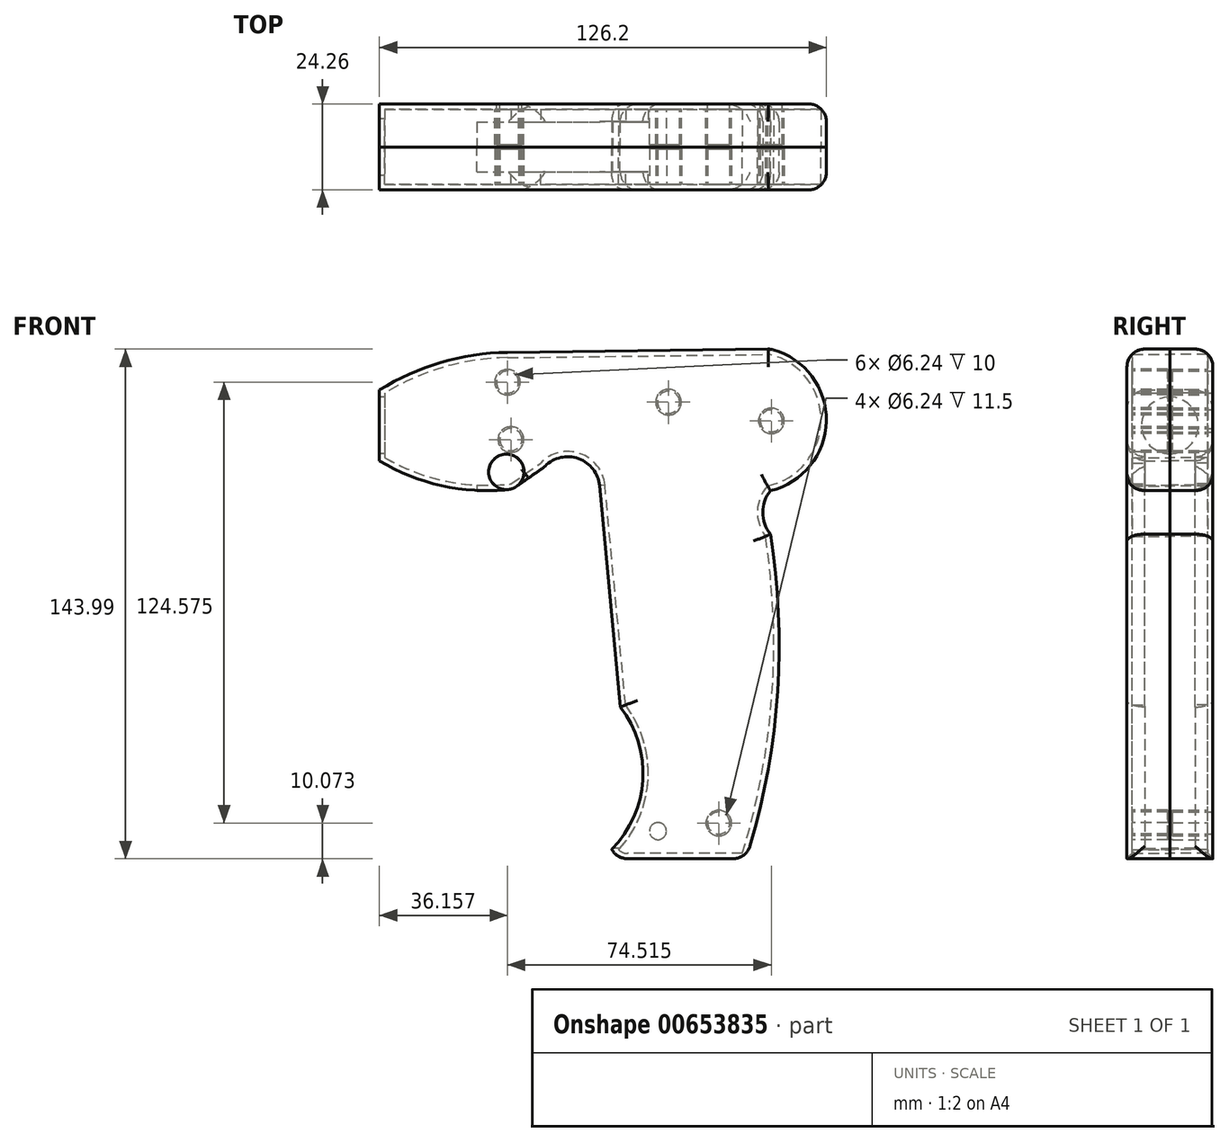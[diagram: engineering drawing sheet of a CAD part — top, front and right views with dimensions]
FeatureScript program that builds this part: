
annotation { "Feature Type Name" : "Feature", "Feature Type Description" : "" }
export const myFeature = defineFeature(function(context is Context, id is Id, definition is map)
    precondition{}
    {
        {
            var Q0;
            Q0=qCreatedBy(makeId("Front.planeOp"),FACE);
            var sketch = newSketch(context, id + "F0", { "sketchPlane" : qUnion([Q0])});
            skLineSegment(sketch, "E0", {"start": v(-46.5, 40.72) * mm, "end": v(-46.5, 20.76) * mm});
            skArc(sketch, "E1", {"start": v(63.9, 12.29) * mm, "mid": v(79.7, 32.29) * mm, "end": v(63.9, 52.29) * mm});
            skPoint(sketch, "E2", {"position": v(65.78, -46.25) * mm});
            skPoint(sketch, "E3", {"position": v(89.04, 165.66) * mm});
            skPoint(sketch, "E4", {"position": v(-8.84, 12.76) * mm});
            skPoint(sketch, "E5", {"position": v(-8.84, 20.76) * mm});
            skPoint(sketch, "E6", {"position": v(79.7, 32.29) * mm});
            skArc(sketch, "E7", {"start": v(63.9, 12.29) * mm, "mid": v(61.71, 6.14) * mm, "end": v(63.9, 0) * mm});
            skArc(sketch, "E8", {"start": v(57.05, -91.71) * mm, "mid": v(65.78, -46.25) * mm, "end": v(63.9, 0) * mm});
            skLineSegment(sketch, "E9", {"start": v(57.05, -91.71) * mm, "end": v(23.56, -91.71) * mm});
            skLineSegment(sketch, "E10", {"start": v(21.52, -48.85) * mm, "end": v(15.66, 13.67) * mm});
            skLineSegment(sketch, "E11", {"start": v(-10.37, 51.36) * mm, "end": v(63.9, 52.29) * mm});
            skPoint(sketch, "E12", {"position": v(57.05, -91.71) * mm});
            skLineSegment(sketch, "E13", {"start": v(-8.84, 12.76) * mm, "end": v(0, 18.96) * mm});
            skArc(sketch, "E14", {"start": v(15.66, 13.67) * mm, "mid": v(9.55, 21.4) * mm, "end": v(0, 18.96) * mm});
            skArc(sketch, "E15", {"start": v(19.1, -89.07) * mm, "mid": v(20.97, -91) * mm, "end": v(23.56, -91.71) * mm});
            skArc(sketch, "E16", {"start": v(19.1, -89.07) * mm, "mid": v(27.84, -69.42) * mm, "end": v(21.52, -48.85) * mm});
            skPoint(sketch, "E17", {"position": v(19.1, -91.71) * mm});
            skArc(sketch, "E18", {"start": v(-46.5, 20.76) * mm, "mid": v(-28.35, 13.58) * mm, "end": v(-8.84, 12.76) * mm});
            skArc(sketch, "E19", {"start": v(-10.37, 51.36) * mm, "mid": v(-29.17, 48.53) * mm, "end": v(-46.5, 40.72) * mm});
            skPoint(sketch, "E20", {"position": v(-10.37, 40.72) * mm});
            skPoint(sketch, "E21", {"position": v(63.9, 32.29) * mm});
            skPoint(sketch, "E22", {"position": v(60.43, -79.71) * mm});
            skPoint(sketch, "E23", {"position": v(40.05, -91.71) * mm});
            skPoint(sketch, "E24", {"position": v(40.05, -79.71) * mm});
            skPoint(sketch, "E25", {"position": v(-46.5, 30.74) * mm});
            skLineSegment(sketch, "E26", {"start": v(78.94, 37.8) * mm, "end": v(79.7, 32.29) * mm});
            skPoint(sketch, "E27", {"position": v(50.96, -79.71) * mm});
            skSolve(sketch);
        }
        {
            var Q0;
            Q0 = qSketchRegion(id + "F0", true);
            extrude(context, id + "F1", {"entities" : qUnion([Q0]), "depth" : 12.13 * mm, "offsetDistance" : 25 * mm});
        }
        {
            var Q0;
            Q0=makeQuery(id+"F1.opExtrude","CAP_FACE",FACE,{"disambiguationData":[OSD([sQuery(id+"F0.wireOp",EDGE,"E0"),sQuery(id+"F0.wireOp",EDGE,"E1"),sQuery(id+"F0.wireOp",EDGE,"E7"),sQuery(id+"F0.wireOp",EDGE,"E8"),sQuery(id+"F0.wireOp",EDGE,"E9"),sQuery(id+"F0.wireOp",EDGE,"E10"),sQuery(id+"F0.wireOp",EDGE,"E11"),sQuery(id+"F0.wireOp",EDGE,"E13"),sQuery(id+"F0.wireOp",EDGE,"E14"),sQuery(id+"F0.wireOp",EDGE,"E15"),sQuery(id+"F0.wireOp",EDGE,"E16"),sQuery(id+"F0.wireOp",EDGE,"E18"),sQuery(id+"F0.wireOp",EDGE,"E19")])],"isStart":true});
            shell(context, id + "F2", {"entities" : qUnion([Q0]), "thickness" : 1.5 * mm});
        }
        {
            var Q0;
            Q0=makeQuery(id+"F1.opExtrude","CAP_EDGE",EDGE,{"disambiguationData":[OSD([sQuery(id+"F0.wireOp",EDGE,"E11")])],"isStart":false});
            fillet(context, id + "F3", {"entities" : qUnion([Q0]), "radius" : 5 * mm, "tangentPropagation" : true, "allowEdgeOverflow" : false});
        }
        {
            var Q0;
            Q0=makeQuery(id+"F1.opExtrude","CAP_EDGE",EDGE,{"disambiguationData":[OSD([sQuery(id+"F0.wireOp",EDGE,"E1")])],"isStart":false});
            var Q1;
            Q1=makeQuery(id+"F1.opExtrude","CAP_EDGE",EDGE,{"disambiguationData":[OSD([sQuery(id+"F0.wireOp",EDGE,"E7")])],"isStart":false});
            var Q2;
            Q2=makeQuery(id+"F1.opExtrude","CAP_EDGE",EDGE,{"disambiguationData":[OSD([sQuery(id+"F0.wireOp",EDGE,"E8")])],"isStart":false});
            var Q3;
            Q3=makeQuery(id+"F1.opExtrude","SWEPT_EDGE",EDGE,{"disambiguationData":[OSD([sQuery(id+"F0.wireOp",EDGE,"E8"),sQuery(id+"F0.wireOp",EDGE,"E9")])]});
            var Q4;
            Q4=makeQuery(id+"F1.opExtrude","SWEPT_EDGE",EDGE,{"disambiguationData":[OSD([sQuery(id+"F0.wireOp",EDGE,"E9"),sQuery(id+"F0.wireOp",EDGE,"E15")])]});
            var Q5;
            Q5=makeQuery(id+"F1.opExtrude","CAP_EDGE",EDGE,{"disambiguationData":[OSD([sQuery(id+"F0.wireOp",EDGE,"E16")])],"isStart":false});
            var Q6;
            Q6=makeQuery(id+"F1.opExtrude","CAP_EDGE",EDGE,{"disambiguationData":[OSD([sQuery(id+"F0.wireOp",EDGE,"E10")])],"isStart":false});
            var Q7;
            Q7=makeQuery(id+"F1.opExtrude","CAP_EDGE",EDGE,{"disambiguationData":[OSD([sQuery(id+"F0.wireOp",EDGE,"E18")])],"isStart":false});
            var Q8;
            Q8=makeQuery(id+"F1.opExtrude","SWEPT_EDGE",EDGE,{"disambiguationData":[OSD([sQuery(id+"F0.wireOp",EDGE,"E13"),sQuery(id+"F0.wireOp",EDGE,"E18")])]});
            var Q9;
            Q9=makeQuery(id+"F1.opExtrude","SWEPT_EDGE",EDGE,{"disambiguationData":[OSD([sQuery(id+"F0.wireOp",EDGE,"E13"),sQuery(id+"F0.wireOp",EDGE,"E14")])]});
            fillet(context, id + "F4", {"entities" : qUnion([Q0, Q1, Q2, Q3, Q4, Q5, Q6, Q7, Q8, Q9]), "radius" : 5 * mm, "tangentPropagation" : true, "allowEdgeOverflow" : false});
        }
        {
            var Q0;
            Q0=makeQuery(id+"F1.opExtrude","SWEPT_FACE",FACE,{"disambiguationData":[OSD([sQuery(id+"F0.wireOp",EDGE,"E0")])]});
            var sketch = newSketch(context, id + "F5", { "sketchPlane" : qUnion([Q0])});
            skCircle(sketch, "E28", {"center": v(0, 30.74) * mm, "radius": 8 * mm});
            skSolve(sketch);
        }
        {
            var Q0;
            {var subQ0=sQuery(id+"F5.wireOp",EDGE,"E28");var subQ1=makeQuery(id+"F1.opExtrude","CAP_EDGE",EDGE,{"disambiguationData":[OSD([sQuery(id+"F0.wireOp",EDGE,"E0")])],"isStart":true});var subQ2=makeQuery(id+"F5.imprint","INTERSECT",VERTEX,{"disambiguationData":[OD(0.0)],"derivedFrom":[subQ1,subQ0]});Q0=makeQuery(id+"F5.imprint","IMPRINT",FACE,{"disambiguationData":[TD([[makeQuery(id+"F5.imprint","IMPRINT",EDGE,{"disambiguationData":[TD([[subQ2,1.0]])],"derivedFrom":subQ0}),1.0]])]});}
            extrude(context, id + "F6", {"entities" : qUnion([Q0]), "operationType" : NewBodyOperationType.REMOVE, "oppositeDirection" : true, "depth" : 25.5 * mm, "offsetDistance" : 25 * mm});
        }
        {
            var Q0;
            Q0=makeQuery(id+"F1.opExtrude","SWEPT_FACE",FACE,{"disambiguationData":[OSD([sQuery(id+"F0.wireOp",EDGE,"E10")])]});
            extrude(context, id + "F7", {"entities" : qUnion([Q0]), "operationType" : NewBodyOperationType.REMOVE, "oppositeDirection" : true, "depth" : 25 * mm, "offsetDistance" : 25 * mm});
        }
        {
            var Q0;
            Q0=qCreatedBy(makeId("Right.planeOp"),FACE);
            var sketch = newSketch(context, id + "F8", { "sketchPlane" : qUnion([Q0])});
            skLineSegment(sketch, "E29.bottom", {"start": v(0, 32.22) * mm, "end": v(-7.06, 32.22) * mm});
            skLineSegment(sketch, "E29.top", {"start": v(0, -88.8) * mm, "end": v(-7.06, -88.8) * mm});
            skLineSegment(sketch, "E29.left", {"start": v(0, 32.22) * mm, "end": v(0, -88.8) * mm});
            skLineSegment(sketch, "E29.right", {"start": v(-7.06, 32.22) * mm, "end": v(-7.06, -88.8) * mm});
            skSolve(sketch);
        }
        {
            var Q0;
            Q0 = qSketchRegion(id + "F8", true);
            extrude(context, id + "F9", {"entities" : qUnion([Q0]), "operationType" : NewBodyOperationType.REMOVE, "depth" : 32 * mm, "offsetDistance" : 25 * mm});
        }
        {
            var Q0;
            Q0=qCreatedBy(makeId("Right.planeOp"),FACE);
            var sketch = newSketch(context, id + "F10", { "sketchPlane" : qUnion([Q0])});
            skLineSegment(sketch, "E30.bottom", {"start": v(-7.06, 30.82) * mm, "end": v(0, 30.82) * mm});
            skLineSegment(sketch, "E30.top", {"start": v(-7.06, -88.82) * mm, "end": v(0, -88.82) * mm});
            skLineSegment(sketch, "E30.left", {"start": v(-7.06, 30.82) * mm, "end": v(-7.06, -88.82) * mm});
            skLineSegment(sketch, "E30.right", {"start": v(0, 30.82) * mm, "end": v(0, -88.82) * mm});
            skSolve(sketch);
        }
        {
            var Q0;
            Q0 = qSketchRegion(id + "F10", true);
            extrude(context, id + "F11", {"entities" : qUnion([Q0]), "operationType" : NewBodyOperationType.REMOVE, "oppositeDirection" : true, "depth" : 19 * mm, "offsetDistance" : 25 * mm});
        }
        {
            var Q0;
            {var subQ0=sQuery(id+"F0.wireOp",EDGE,"Wmh0p9kF-q8zf-B4fM-R1G6-9XajL4hFd1sJ");var subQ1=sQuery(id+"F0.wireOp",EDGE,"YQ1TRmyh-YhWL-v7ih-TSwX-I9xARRby4IsQ");var subQ2=sQuery(id+"F0.wireOp",EDGE,"R5RoQ8MB-LLDK-kKnW-gyy2-uW1s3o3SLSVy");var subQ3=sQuery(id+"F0.wireOp",EDGE,"7nFK0jpW-g7ep-zzM4-bCTe-Nh05jLanKP2S");var subQ4=sQuery(id+"F0.wireOp",EDGE,"E19");var subQ5=sQuery(id+"F0.wireOp",EDGE,"E18");var subQ6=sQuery(id+"F0.wireOp",EDGE,"E16");var subQ7=sQuery(id+"F0.wireOp",EDGE,"E15");var subQ8=sQuery(id+"F0.wireOp",EDGE,"E14");var subQ9=sQuery(id+"F0.wireOp",EDGE,"E13");var subQ10=sQuery(id+"F0.wireOp",EDGE,"E11");var subQ11=sQuery(id+"F0.wireOp",EDGE,"E10");var subQ12=sQuery(id+"F0.wireOp",EDGE,"E9");var subQ13=sQuery(id+"F0.wireOp",EDGE,"E8");var subQ14=sQuery(id+"F0.wireOp",EDGE,"E7");var subQ15=sQuery(id+"F0.wireOp",EDGE,"E1");var subQ16=sQuery(id+"F0.wireOp",EDGE,"E0");Q0=makeQuery(id+"F2.opShell","OFFSET_FACE",FACE,{"disambiguationData":[OSD([subQ16,subQ15,subQ14,subQ13,subQ12,subQ11,subQ10,subQ9,subQ8,subQ7,subQ6,subQ5,subQ4,subQ3,subQ2,subQ1,subQ0]),TDD([makeQuery(id+"F1.opExtrude","CAP_FACE",FACE,{"disambiguationData":[OSD([subQ16,subQ15,subQ14,subQ13,subQ12,subQ11,subQ10,subQ9,subQ8,subQ7,subQ6,subQ5,subQ4,subQ3,subQ2,subQ1,subQ0])],"isStart":false})])]});}
            var sketch = newSketch(context, id + "F12", { "sketchPlane" : qUnion([Q0])});
            skCircle(sketch, "E31", {"center": v(-32.15, -83.92) * mm, "radius": 2.4 * mm});
            skCircle(sketch, "E32", {"center": v(-35.12, 37.29) * mm, "radius": 3.12 * mm});
            skPoint(sketch, "E33", {"position": v(10.35, 42.94) * mm});
            skPoint(sketch, "E34", {"position": v(9.4, 26.72) * mm});
            skPoint(sketch, "E35", {"position": v(-64.16, 32.01) * mm});
            skPoint(sketch, "E36", {"position": v(-49.3, -81.64) * mm});
            skCircle(sketch, "E37", {"center": v(-49.3, -81.64) * mm, "radius": 3.12 * mm});
            skCircle(sketch, "E38", {"center": v(9.4, 26.72) * mm, "radius": 3.12 * mm});
            skCircle(sketch, "E39", {"center": v(10.35, 42.94) * mm, "radius": 3.12 * mm});
            skCircle(sketch, "E40", {"center": v(-64.16, 32.01) * mm, "radius": 3.12 * mm});
            skCircle(sketch, "E41", {"center": v(-64.16, 32.01) * mm, "radius": 3.62 * mm});
            skCircle(sketch, "E42", {"center": v(-35.12, 37.29) * mm, "radius": 3.62 * mm});
            skCircle(sketch, "E43", {"center": v(10.35, 42.94) * mm, "radius": 3.62 * mm});
            skCircle(sketch, "E44", {"center": v(9.4, 26.72) * mm, "radius": 3.62 * mm});
            skCircle(sketch, "E45", {"center": v(-49.3, -81.64) * mm, "radius": 3.62 * mm});
            skSolve(sketch);
        }
        {
            var Q0;
            Q0 = qSketchRegion(id + "F12", true);
            extrude(context, id + "F13", {"entities" : qUnion([Q0]), "operationType" : NewBodyOperationType.ADD, "depth" : 10 * mm, "offsetDistance" : 25 * mm});
        }
        {
            var Q0;
            Q0=makeQuery(id+"F1.opExtrude","SWEPT_BODY",BODY,{"disambiguationData":[OSD([sQuery(id+"F0.wireOp",EDGE,"E0"),sQuery(id+"F0.wireOp",EDGE,"E1"),sQuery(id+"F0.wireOp",EDGE,"E7"),sQuery(id+"F0.wireOp",EDGE,"E8"),sQuery(id+"F0.wireOp",EDGE,"E9"),sQuery(id+"F0.wireOp",EDGE,"E10"),sQuery(id+"F0.wireOp",EDGE,"E11"),sQuery(id+"F0.wireOp",EDGE,"E13"),sQuery(id+"F0.wireOp",EDGE,"E14"),sQuery(id+"F0.wireOp",EDGE,"E15"),sQuery(id+"F0.wireOp",EDGE,"E16"),sQuery(id+"F0.wireOp",EDGE,"E18"),sQuery(id+"F0.wireOp",EDGE,"E19"),sQuery(id+"F0.wireOp",EDGE,"7nFK0jpW-g7ep-zzM4-bCTe-Nh05jLanKP2S"),sQuery(id+"F0.wireOp",EDGE,"R5RoQ8MB-LLDK-kKnW-gyy2-uW1s3o3SLSVy"),sQuery(id+"F0.wireOp",EDGE,"YQ1TRmyh-YhWL-v7ih-TSwX-I9xARRby4IsQ"),sQuery(id+"F0.wireOp",EDGE,"kS4eHpj9-8okb-2U2w-MQt4-eAn52PG1cgjK")])]});
            transform(context, id + "F14", {"entities" : qUnion([Q0]), "transformType" : TransformType.TRANSLATION_3D, "dx" : 0 * mm, "dy" : 187.3 * mm, "dz" : 0 * mm, "makeCopy" : true});
        }
        {
            var Q0;
            {var subQ0=sQuery(id+"F0.wireOp",EDGE,"kS4eHpj9-8okb-2U2w-MQt4-eAn52PG1cgjK");var subQ1=sQuery(id+"F0.wireOp",EDGE,"YQ1TRmyh-YhWL-v7ih-TSwX-I9xARRby4IsQ");var subQ2=sQuery(id+"F0.wireOp",EDGE,"R5RoQ8MB-LLDK-kKnW-gyy2-uW1s3o3SLSVy");var subQ3=sQuery(id+"F0.wireOp",EDGE,"7nFK0jpW-g7ep-zzM4-bCTe-Nh05jLanKP2S");var subQ4=sQuery(id+"F0.wireOp",EDGE,"E19");var subQ5=sQuery(id+"F0.wireOp",EDGE,"E18");var subQ6=sQuery(id+"F0.wireOp",EDGE,"E16");var subQ7=sQuery(id+"F0.wireOp",EDGE,"E15");var subQ8=sQuery(id+"F0.wireOp",EDGE,"E14");var subQ9=sQuery(id+"F0.wireOp",EDGE,"E13");var subQ10=sQuery(id+"F0.wireOp",EDGE,"E11");var subQ11=sQuery(id+"F0.wireOp",EDGE,"E10");var subQ12=sQuery(id+"F0.wireOp",EDGE,"E9");var subQ13=sQuery(id+"F0.wireOp",EDGE,"E8");var subQ14=sQuery(id+"F0.wireOp",EDGE,"E7");var subQ15=sQuery(id+"F0.wireOp",EDGE,"E1");var subQ16=sQuery(id+"F0.wireOp",EDGE,"E0");Q0=makeQuery(id+"F14.opPattern","COPY",FACE,{"derivedFrom":makeQuery(id+"F2.opShell","OFFSET_FACE",FACE,{"disambiguationData":[OSD([subQ16,subQ15,subQ14,subQ13,subQ12,subQ11,subQ10,subQ9,subQ8,subQ7,subQ6,subQ5,subQ4,subQ3,subQ2,subQ1,subQ0]),TDD([makeQuery(id+"F1.opExtrude","CAP_FACE",FACE,{"disambiguationData":[OSD([subQ16,subQ15,subQ14,subQ13,subQ12,subQ11,subQ10,subQ9,subQ8,subQ7,subQ6,subQ5,subQ4,subQ3,subQ2,subQ1,subQ0])],"isStart":false})])]}),"instanceName":"1"});}
            var sketch = newSketch(context, id + "F15", { "sketchPlane" : qUnion([Q0])});
            skSolve(sketch);
        }
        {
            var Q0;
            Q0=makeQuery(id+"FIR2Xu8sqB9YDc9_1.opExtrude","SWEPT_BODY",BODY,{"disambiguationData":[OSD([sQuery(id+"F12.wireOp",EDGE,"E40")])]});
            var Q1;
            Q1=makeQuery(id+"F14.opPattern","COPY",BODY,{"derivedFrom":makeQuery(id+"F1.opExtrude","SWEPT_BODY",BODY,{"disambiguationData":[OSD([sQuery(id+"F0.wireOp",EDGE,"E0"),sQuery(id+"F0.wireOp",EDGE,"E1"),sQuery(id+"F0.wireOp",EDGE,"E7"),sQuery(id+"F0.wireOp",EDGE,"E8"),sQuery(id+"F0.wireOp",EDGE,"E9"),sQuery(id+"F0.wireOp",EDGE,"E10"),sQuery(id+"F0.wireOp",EDGE,"E11"),sQuery(id+"F0.wireOp",EDGE,"E13"),sQuery(id+"F0.wireOp",EDGE,"E14"),sQuery(id+"F0.wireOp",EDGE,"E15"),sQuery(id+"F0.wireOp",EDGE,"E16"),sQuery(id+"F0.wireOp",EDGE,"E18"),sQuery(id+"F0.wireOp",EDGE,"E19")])]}),"instanceName":"1"});
            deleteBodies(context, id + "F16", {"entities" : qUnion([Q0, Q1])});
        }
        {
            var Q0;
            Q0=makeQuery(id+"F1.opExtrude","SWEPT_BODY",BODY,{"disambiguationData":[OSD([sQuery(id+"F0.wireOp",EDGE,"E0"),sQuery(id+"F0.wireOp",EDGE,"E1"),sQuery(id+"F0.wireOp",EDGE,"E7"),sQuery(id+"F0.wireOp",EDGE,"E8"),sQuery(id+"F0.wireOp",EDGE,"E9"),sQuery(id+"F0.wireOp",EDGE,"E10"),sQuery(id+"F0.wireOp",EDGE,"E11"),sQuery(id+"F0.wireOp",EDGE,"E13"),sQuery(id+"F0.wireOp",EDGE,"E14"),sQuery(id+"F0.wireOp",EDGE,"E15"),sQuery(id+"F0.wireOp",EDGE,"E16"),sQuery(id+"F0.wireOp",EDGE,"E18"),sQuery(id+"F0.wireOp",EDGE,"E19")])]});
            var Q1;
            {var subQ0=sQuery(id+"F0.wireOp",EDGE,"E16");var subQ1=sQuery(id+"F0.wireOp",EDGE,"E7");var subQ2=sQuery(id+"F0.wireOp",EDGE,"E11");var subQ3=sQuery(id+"F0.wireOp",EDGE,"E9");var subQ4=sQuery(id+"F0.wireOp",EDGE,"E15");var subQ5=sQuery(id+"F0.wireOp",EDGE,"E1");var subQ6=sQuery(id+"F0.wireOp",EDGE,"E0");var subQ7=sQuery(id+"F0.wireOp",EDGE,"E8");var subQ8=sQuery(id+"F0.wireOp",EDGE,"E19");var subQ9=sQuery(id+"F0.wireOp",EDGE,"E10");Q1=makeQuery(id+"F7.boolean.opBoolean","SPLIT",FACE,{"disambiguationData":[TD([makeQuery(id+"F1.opExtrude","SWEPT_FACE",FACE,{"disambiguationData":[OSD([subQ5])]})])],"derivedFrom":makeQuery(id+"F1.opExtrude","CAP_FACE",FACE,{"disambiguationData":[OSD([subQ6,subQ5,subQ1,subQ7,subQ3,subQ9,subQ2,sQuery(id+"F0.wireOp",EDGE,"E13"),sQuery(id+"F0.wireOp",EDGE,"E14"),subQ4,subQ0,sQuery(id+"F0.wireOp",EDGE,"E18"),subQ8])],"isStart":true})});}
            mirror(context, id + "F17", {"entities" : qUnion([Q0]), "mirrorPlane" : qUnion([Q1])});
        }
        {
            var Q0;
            {var subQ0=sQuery(id+"F0.wireOp",EDGE,"E15");var subQ1=sQuery(id+"F0.wireOp",EDGE,"E14");var subQ2=sQuery(id+"F0.wireOp",EDGE,"E13");var subQ3=sQuery(id+"F0.wireOp",EDGE,"E11");var subQ4=sQuery(id+"F0.wireOp",EDGE,"E10");var subQ5=sQuery(id+"F0.wireOp",EDGE,"E9");var subQ6=sQuery(id+"F0.wireOp",EDGE,"E0");var subQ7=sQuery(id+"F0.wireOp",EDGE,"E1");var subQ8=sQuery(id+"F0.wireOp",EDGE,"E7");var subQ9=sQuery(id+"F0.wireOp",EDGE,"E8");var subQ10=sQuery(id+"F0.wireOp",EDGE,"E16");var subQ11=sQuery(id+"F0.wireOp",EDGE,"E18");var subQ12=sQuery(id+"F0.wireOp",EDGE,"E19");Q0=makeQuery(id+"F17.opPattern","COPY",FACE,{"derivedFrom":makeQuery(id+"F13.boolean.opBoolean","SPLIT",FACE,{"disambiguationData":[TD([makeQuery(id+"F2.opShell","OFFSET_FACE",FACE,{"disambiguationData":[OSD([subQ6])]})])],"derivedFrom":makeQuery(id+"F2.opShell","OFFSET_FACE",FACE,{"disambiguationData":[OSD([subQ6,subQ7,subQ8,subQ9,subQ5,subQ4,subQ3,subQ2,subQ1,subQ0,subQ10,subQ11,subQ12])]})}),"instanceName":"1"});}
            var sketch = newSketch(context, id + "F18", { "sketchPlane" : qUnion([Q0])});
            skCircle(sketch, "E46", {"center": v(-10.35, 42.94) * mm, "radius": 3.12 * mm});
            skCircle(sketch, "E47", {"center": v(-9.4, 26.72) * mm, "radius": 3.12 * mm});
            skCircle(sketch, "E48", {"center": v(64.16, 32.01) * mm, "radius": 3.12 * mm});
            skCircle(sketch, "E49", {"center": v(49.3, -81.64) * mm, "radius": 3.12 * mm});
            skSolve(sketch);
        }
        {
            var Q0;
            Q0 = qSketchRegion(id + "F18", true);
            extrude(context, id + "F19", {"entities" : qUnion([Q0]), "operationType" : NewBodyOperationType.REMOVE, "oppositeDirection" : true, "depth" : 92.7 * mm, "offsetDistance" : 25 * mm});
        }
    });
